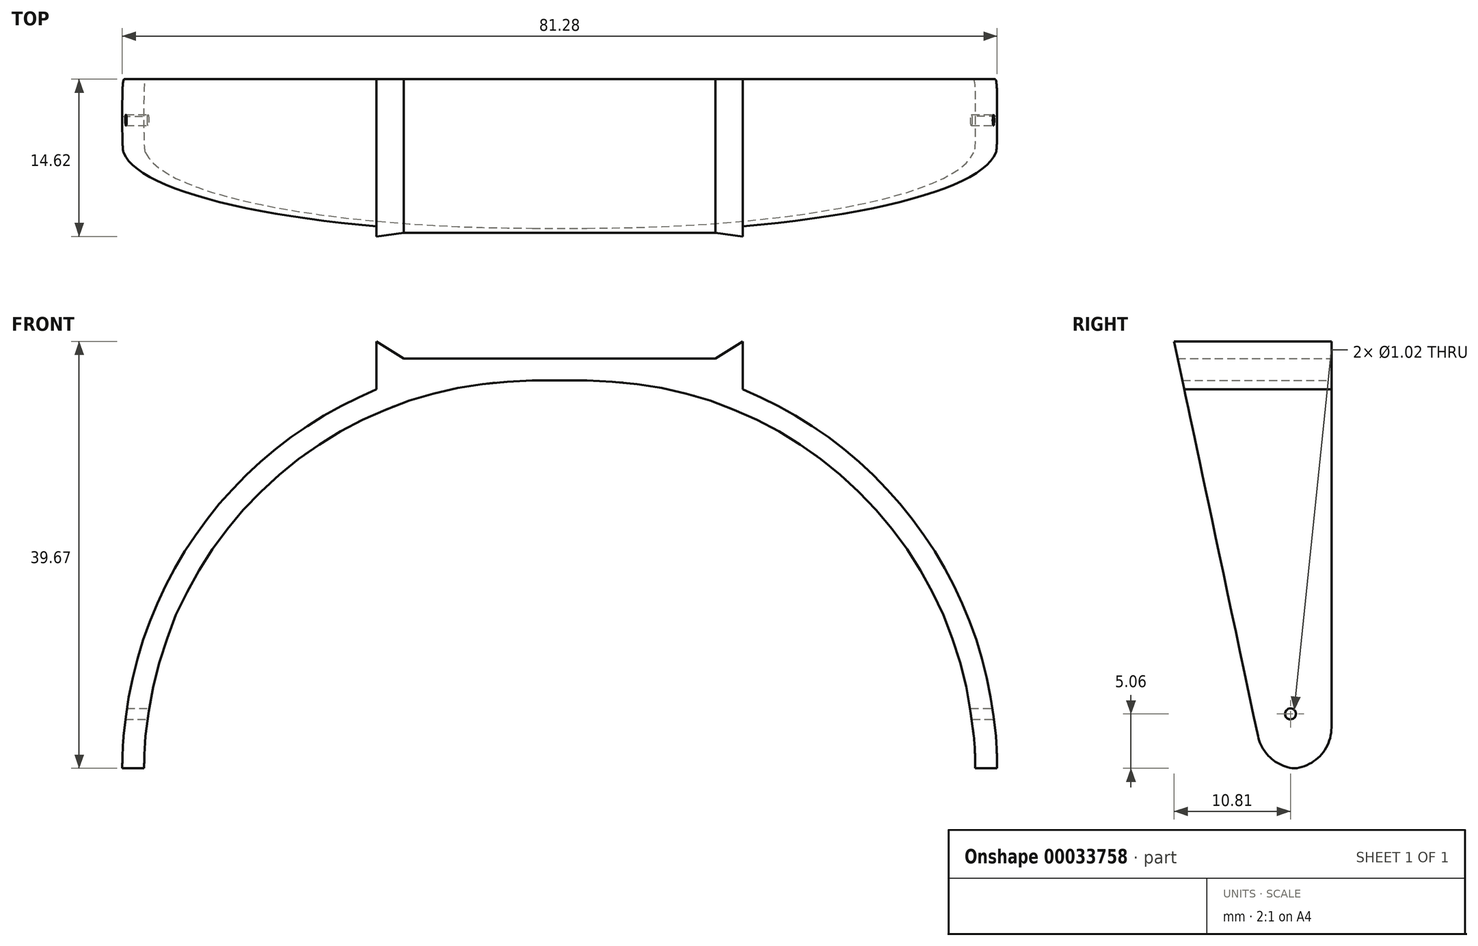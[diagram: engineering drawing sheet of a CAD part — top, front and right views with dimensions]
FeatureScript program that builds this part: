
annotation { "Feature Type Name" : "Feature", "Feature Type Description" : "" }
export const myFeature = defineFeature(function(context is Context, id is Id, definition is map)
    precondition{}
    {
        {
            var Q0;
            Q0=qCreatedBy(makeId("Front.planeOp"),FACE);
            var sketch = newSketch(context, id + "F0", { "sketchPlane" : qUnion([Q0])});
            skLineSegment(sketch, "E0", {"start": v(0, 0) * mm, "end": v(0, -90.6) * mm, "construction": true});
            skLineSegment(sketch, "E1", {"start": v(0, 0) * mm, "end": v(-14.48, 0) * mm});
            skArc(sketch, "E2", {"start": v(-17.02, -2.86) * mm, "mid": v(-34.19, -16.89) * mm, "end": v(-40.64, -38.1) * mm});
            skLineSegment(sketch, "E3", {"start": v(-38.6, -38.1) * mm, "end": v(-40.64, -38.1) * mm});
            skArc(sketch, "E4.0", {"start": v(-2.54, -2.03) * mm, "mid": v(-28.04, -12.6) * mm, "end": v(-38.6, -38.1) * mm});
            skLineSegment(sketch, "E4.1", {"start": v(0, -2.03) * mm, "end": v(-2.54, -2.03) * mm});
            skLineSegment(sketch, "E5.MirrorCS", {"start": v(0, 0) * mm, "end": v(14.48, 0) * mm});
            skLineSegment(sketch, "E6.MirrorCS", {"start": v(0, -2.03) * mm, "end": v(2.54, -2.03) * mm});
            skArc(sketch, "E7.MirrorCS", {"start": v(2.54, -2.03) * mm, "mid": v(28.04, -12.6) * mm, "end": v(38.6, -38.1) * mm});
            skArc(sketch, "E8.MirrorCS", {"start": v(17.02, -2.86) * mm, "mid": v(34.19, -16.89) * mm, "end": v(40.64, -38.1) * mm});
            skLineSegment(sketch, "E9.MirrorCS", {"start": v(38.6, -38.1) * mm, "end": v(40.64, -38.1) * mm});
            skLineSegment(sketch, "E10", {"start": v(-17.02, 0) * mm, "end": v(-17.02, 1.59) * mm});
            skLineSegment(sketch, "E11", {"start": v(-17.02, 1.59) * mm, "end": v(-14.48, 0) * mm});
            skLineSegment(sketch, "E12.trimOffspring", {"start": v(-2.54, 0) * mm, "end": v(-17.02, 0) * mm});
            skLineSegment(sketch, "E13.MirrorCS", {"start": v(17.02, 1.59) * mm, "end": v(14.48, 0) * mm});
            skLineSegment(sketch, "E14.MirrorCS", {"start": v(17.02, 0) * mm, "end": v(17.02, 1.59) * mm});
            skLineSegment(sketch, "E15.trimOffspring", {"start": v(2.54, 0) * mm, "end": v(17.02, 0) * mm});
            skLineSegment(sketch, "E16", {"start": v(-17.02, 0) * mm, "end": v(-17.02, -2.86) * mm});
            skLineSegment(sketch, "E17", {"start": v(17.02, 0) * mm, "end": v(17.02, -2.86) * mm});
            skPoint(sketch, "E18.orphan", {"position": v(2.54, 0) * mm});
            skSolve(sketch);
        }
        {
            var Q0;
            Q0 = qSketchRegion(id + "F0", true);
            extrude(context, id + "F1", {"entities" : qUnion([Q0]), "depth" : 25.4 * mm});
        }
        {
            var Q0;
            Q0=qCreatedBy(makeId("Right.planeOp"),FACE);
            var sketch = newSketch(context, id + "F2", { "sketchPlane" : qUnion([Q0])});
            skLineSegment(sketch, "E19", {"start": v(-3.49, -50.8) * mm, "end": v(-30.48, 76.2) * mm});
            skLineSegment(sketch, "E20", {"start": v(-30.48, 76.2) * mm, "end": v(-30.48, -50.8) * mm});
            skLineSegment(sketch, "E21", {"start": v(-30.48, -50.8) * mm, "end": v(-3.49, -50.8) * mm});
            skSolve(sketch);
        }
        {
            var Q0;
            Q0 = qSketchRegion(id + "F2", true);
            extrude(context, id + "F3", {"entities" : qUnion([Q0]), "operationType" : NewBodyOperationType.REMOVE, "endBound" : BoundingType.THROUGH_ALL, "oppositeDirection" : true, "depth" : 25.4 * mm, "hasSecondDirection" : true, "secondDirectionBound" : SecondDirectionBoundingType.THROUGH_ALL, "secondDirectionOppositeDirection" : false, "secondDirectionDepth" : 25.4 * mm});
        }
        {
            var Q0;
            Q0=qCreatedBy(makeId("Right.planeOp"),FACE);
            var sketch = newSketch(context, id + "F4", { "sketchPlane" : qUnion([Q0])});
            skCircle(sketch, "E22", {"center": v(-3.81, -33.02) * mm, "radius": 0.5 * mm});
            skSolve(sketch);
        }
        {
            var Q0;
            Q0 = qSketchRegion(id + "F4", true);
            extrude(context, id + "F5", {"entities" : qUnion([Q0]), "operationType" : NewBodyOperationType.REMOVE, "endBound" : BoundingType.THROUGH_ALL, "oppositeDirection" : true, "depth" : 25.4 * mm, "hasSecondDirection" : true, "secondDirectionBound" : SecondDirectionBoundingType.THROUGH_ALL, "secondDirectionOppositeDirection" : false, "secondDirectionDepth" : 25.4 * mm});
        }
        {
            var Q0;
            Q0=makeQuery(id+"F3.boolean.opBoolean","INTERSECT",EDGE,{"derivedFrom":[makeQuery(id+"F1.opExtrude","SWEPT_FACE",FACE,{"disambiguationData":[OSD([sQuery(id+"F0.wireOp",EDGE,"E9.MirrorCS")])]}),makeQuery(id+"F3.opExtrude","SWEPT_FACE",FACE,{"disambiguationData":[OSD([sQuery(id+"F2.wireOp",EDGE,"E19")])]})]});
            var Q1;
            Q1=makeQuery(id+"F1.opExtrude","CAP_EDGE",EDGE,{"disambiguationData":[OSD([sQuery(id+"F0.wireOp",EDGE,"E9.MirrorCS")])],"isStart":true});
            var Q2;
            Q2=makeQuery(id+"F1.opExtrude","CAP_EDGE",EDGE,{"disambiguationData":[OSD([sQuery(id+"F0.wireOp",EDGE,"E3")])],"isStart":true});
            var Q3;
            Q3=makeQuery(id+"F3.boolean.opBoolean","INTERSECT",EDGE,{"derivedFrom":[makeQuery(id+"F1.opExtrude","SWEPT_FACE",FACE,{"disambiguationData":[OSD([sQuery(id+"F0.wireOp",EDGE,"E3")])]}),makeQuery(id+"F3.opExtrude","SWEPT_FACE",FACE,{"disambiguationData":[OSD([sQuery(id+"F2.wireOp",EDGE,"E19")])]})]});
            fillet(context, id + "F6", {"entities" : qUnion([Q0, Q1, Q2, Q3]), "radius" : 3.8 * mm, "tangentPropagation" : true, "allowEdgeOverflow" : false});
        }
    });
